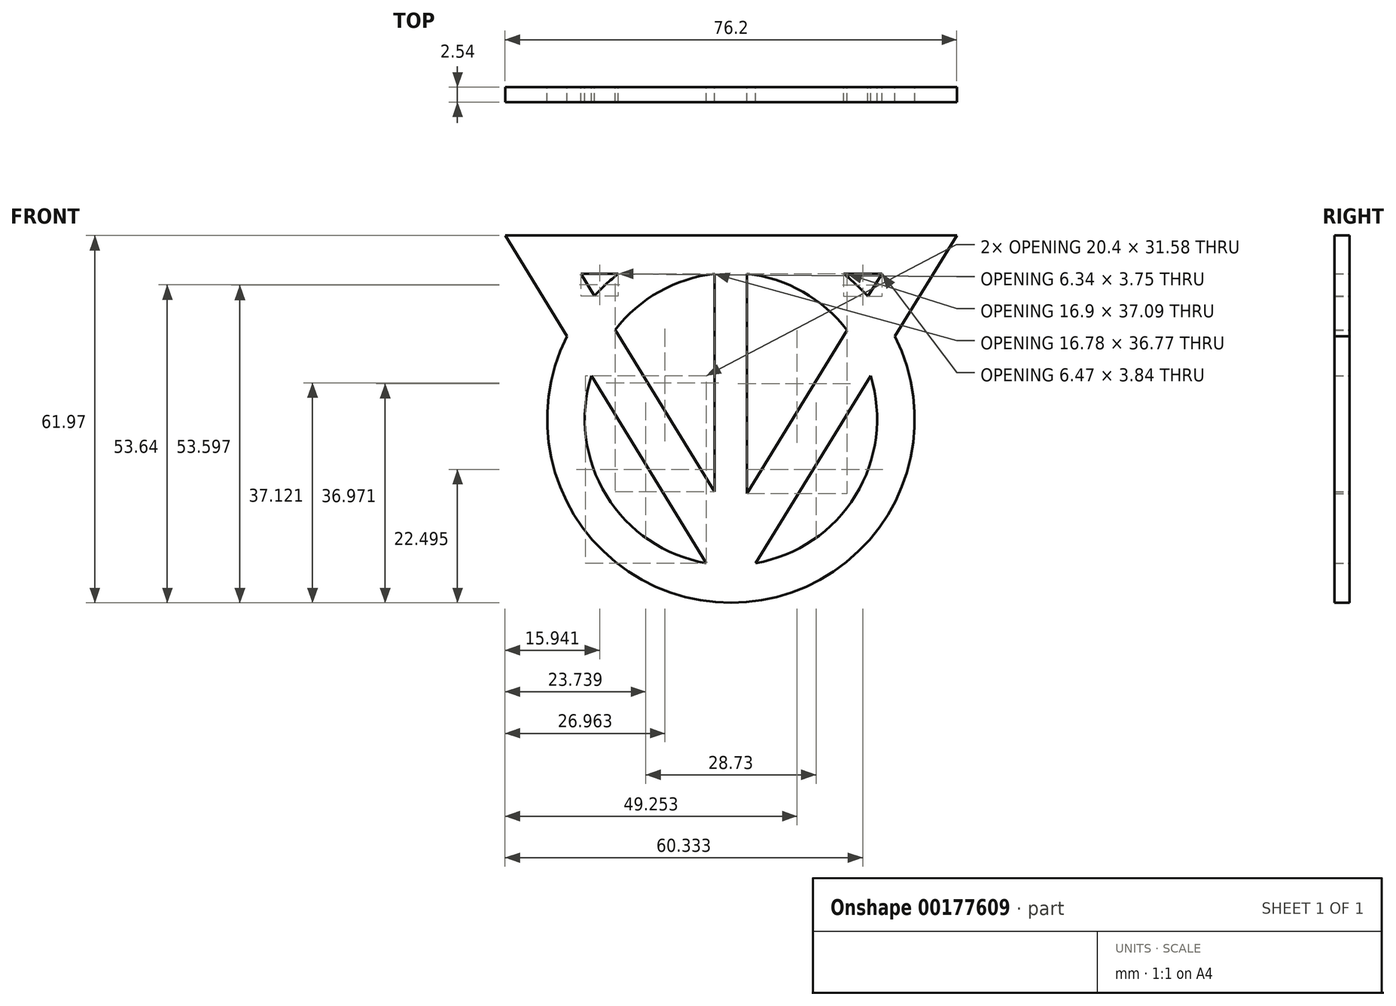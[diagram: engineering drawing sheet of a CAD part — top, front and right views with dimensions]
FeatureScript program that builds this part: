
annotation { "Feature Type Name" : "Feature", "Feature Type Description" : "" }
export const myFeature = defineFeature(function(context is Context, id is Id, definition is map)
    precondition{}
    {
        {
            var Q0;
            Q0=qCreatedBy(makeId("Front.planeOp"),FACE);
            var sketch = newSketch(context, id + "F0", { "sketchPlane" : qUnion([Q0])});
            skArc(sketch, "E0", {"start": v(-17.82, 4.6) * mm, "mid": v(9.85, -40.38) * mm, "end": v(37.53, 4.6) * mm});
            skArc(sketch, "E1", {"start": v(-13.7, -2.1) * mm, "mid": v(-11.16, -22.28) * mm, "end": v(5.69, -33.68) * mm});
            skLineSegment(sketch, "E2", {"start": v(9.85, 21.6) * mm, "end": v(47.95, 21.6) * mm});
            skLineSegment(sketch, "E3", {"start": v(9.85, 21.6) * mm, "end": v(-28.25, 21.6) * mm});
            skLineSegment(sketch, "E4", {"start": v(-28.25, 21.6) * mm, "end": v(-17.82, 4.6) * mm});
            skLineSegment(sketch, "E5", {"start": v(9.85, -40.46) * mm, "end": v(9.9, -40.38) * mm});
            skLineSegment(sketch, "E6", {"start": v(9.85, -40.46) * mm, "end": v(9.85, -40.38) * mm});
            skLineSegment(sketch, "E7", {"start": v(-15.48, 15.14) * mm, "end": v(-9.14, 15.14) * mm});
            skLineSegment(sketch, "E8", {"start": v(35.32, 15.14) * mm, "end": v(32.96, 11.3) * mm});
            skLineSegment(sketch, "E9", {"start": v(-15.48, 15.14) * mm, "end": v(-13.18, 11.38) * mm});
            skLineSegment(sketch, "E10.trimOffspring", {"start": v(-9.67, 5.68) * mm, "end": v(7.1, -21.65) * mm});
            skLineSegment(sketch, "E11.trimOffspring", {"start": v(28.85, 15.14) * mm, "end": v(35.32, 15.14) * mm});
            skLineSegment(sketch, "E12.trimOffspring", {"start": v(29.46, 5.58) * mm, "end": v(12.55, -21.95) * mm});
            skLineSegment(sketch, "E13.trimOffspring", {"start": v(-13.7, -2.1) * mm, "end": v(5.69, -33.68) * mm});
            skLineSegment(sketch, "E14.trimOffspring", {"start": v(9.85, -40.38) * mm, "end": v(9.85, -40.46) * mm});
            skArc(sketch, "E15.trimOffspring", {"start": v(14.02, -33.68) * mm, "mid": v(30.87, -22.28) * mm, "end": v(33.41, -2.1) * mm});
            skLineSegment(sketch, "E16.trimOffspring", {"start": v(9.8, -40.38) * mm, "end": v(9.85, -40.46) * mm});
            skLineSegment(sketch, "E17.trimOffspring", {"start": v(14.02, -33.68) * mm, "end": v(33.41, -2.1) * mm});
            skArc(sketch, "E18.trimOffspring", {"start": v(32.96, 11.3) * mm, "mid": v(31, 13.31) * mm, "end": v(28.85, 15.14) * mm});
            skArc(sketch, "E19.trimOffspring", {"start": v(29.46, 5.58) * mm, "mid": v(21.98, 12.1) * mm, "end": v(12.55, 15.13) * mm});
            skLineSegment(sketch, "E20.trimOffspring", {"start": v(37.53, 4.6) * mm, "end": v(47.95, 21.6) * mm});
            skArc(sketch, "E21.trimOffspring", {"start": v(11.47, 21.6) * mm, "mid": v(9.85, 21.63) * mm, "end": v(8.24, 21.6) * mm});
            skArc(sketch, "E22.trimOffspring", {"start": v(-9.14, 15.14) * mm, "mid": v(-11.24, 13.35) * mm, "end": v(-13.18, 11.38) * mm});
            skLineSegment(sketch, "E23", {"start": v(7.1, 15.13) * mm, "end": v(7.1, -21.65) * mm});
            skLineSegment(sketch, "E24", {"start": v(12.55, 15.13) * mm, "end": v(12.55, -21.95) * mm});
            skArc(sketch, "E25.trimOffspring", {"start": v(7.1, 15.13) * mm, "mid": v(-2.25, 12.1) * mm, "end": v(-9.67, 5.68) * mm});
            skPoint(sketch, "E26.orphan", {"position": v(9.92, -26.24) * mm});
            skPoint(sketch, "E27.orphan", {"position": v(7.1, -26.24) * mm});
            skPoint(sketch, "E28.orphan", {"position": v(12.55, -26.24) * mm});
            skSolve(sketch);
        }
        {
            var Q0;
            Q0=makeQuery(id+"F0.imprint","IMPRINT",FACE,{"disambiguationData":[TD([[makeQuery(id+"F0.imprint","IMPRINT",EDGE,{"derivedFrom":sQuery(id+"F0.wireOp",EDGE,"E1")}),-1.0]])]});
            extrude(context, id + "F1", {"entities" : qUnion([Q0]), "depth" : 2.54 * mm});
        }
    });
